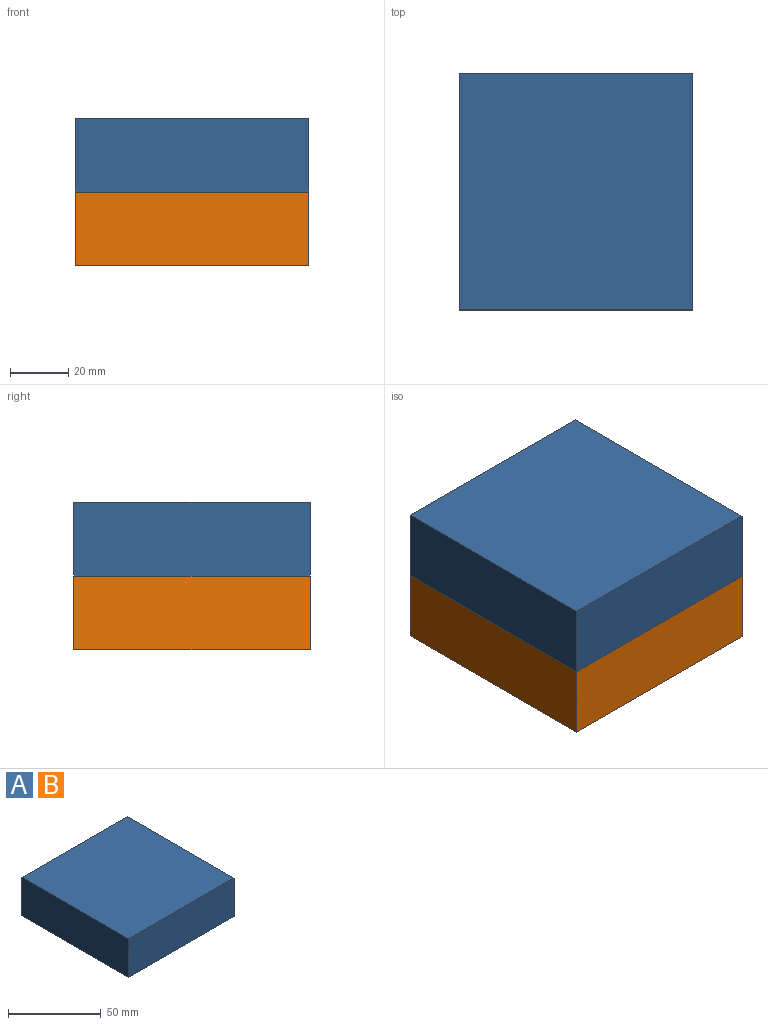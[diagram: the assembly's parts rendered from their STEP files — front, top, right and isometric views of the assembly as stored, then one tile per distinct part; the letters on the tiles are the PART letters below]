
ASSEMBLY  parts=2 mates=1
PART A: 6 faces, bbox 80.2x81.1x25.4 mm
  f0: plane 80.2x25.4mm, normal (0,-1,0), area 2037mm2, adj f1,f3,f4,f5
  f1: plane 81.11x25.4mm, normal (1,0,0), area 2060.1mm2, adj f0,f2,f4,f5
  f2: plane 80.2x25.4mm, normal (0,1,0), area 2037mm2, adj f1,f3,f4,f5
  f3: plane 81.11x25.4mm, normal (-1,0,0), area 2060.1mm2, adj f0,f2,f4,f5
  f4: plane 81.11x80.2mm, normal (0,0,1), area 6504.4mm2, adj f0,f1,f2,f3
  f5: plane 81.11x80.2mm, normal (0,0,-1), area 6504.4mm2, adj f0,f1,f2,f3
PART B: same geometry as A
PLACE A t=(-26.21,-2.85,31.13)mm
PLACE B t=(-26.21,-2.85,5.73)mm
MATE fastened A.f5 <-> B.f4  axis (0,0,-1) through (-26.21,-2.85,31.13)mm
